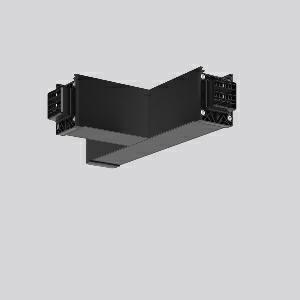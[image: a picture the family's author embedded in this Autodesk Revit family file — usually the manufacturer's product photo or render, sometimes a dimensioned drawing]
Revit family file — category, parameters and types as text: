
# Revit family: linedo_t-verbindung_982774_003_2_b572
name_source: partatom
category: Lighting Fixtures
units: mm (PartAtom-declared; Revit-internal decimal feet)

## family parameters
Cut with Voids When Loaded = No
Host = Face
Light Source = No
Part Type = Normal
Room Calculation Point = No
Round Connector Dimension = Use Diameter
Shared = No

## types (1)
- LINEDO T-Verbindung
    Apparent Load = 0 VA
    Default Elevation = 1800 mm
    Description = Series: LINEDO
T-connector, 14-pole, connection plug / socket - plug. Housing: extruded aluminium profile, powder-coated. Cover made of plastic, surface like housing. LINEDO plug system, plastic, black. Easy connection for rigid or flexible wires. 5 membrane cable entries (2 x M20 and 3 x M25). Suitable for power supply in 7-pole version. Ready prewired. Colour-coded individual cables enable easy electromechanical separation.
Colour: jet black (RAL 9005)
Length: 330 mm
Width: 204 mm
Height: 76 mm
Weight: 1070 g
    Height = 76 mm
    Lamp = 0 x
    Length = 331 mm
    Luminous efficacy = 0 lm/W
    Manufacturer = RZB
    ModVariant = No
    Model = 982774.003.2
    Mounting Place = Ceiling
    Mounting Type = Surface mounted
    Number of Poles = 1
    OnlyDefault = Yes
    Power Factor = 1
    Product Name = LINEDO T-Verbindung
    Product group = Surface mounted continuous line luminaire system
    ProductGroupID = 310
    Protection Class = Protection class I
    Protection Degree = Degree of protection
    RLX_Detail_Level = 1
    RLX_Emergency_Light_Flux = 0 lm
    RLX_Emergency_Type = 0
    RLX_Emergency_Type_DB = No
    RlxData = <blob elided: 20469 chars, md5=bdd1d6c0>
    Standby Power = 0 W
    System Light Flux = 0 lm
    System Power = 0 W
    Type Comments = Product without accessories
    Type Image = 982774.003.2.jpg
    URL = http://relux.com
    VarID = ---
    Voltage = 0 V
    Weight = 0.00 kg
    Width = 204 mm

## geometry (parser evidence)
native form markers: Blend x4, Sweep x12
no freeform markers — native parametric forms only
